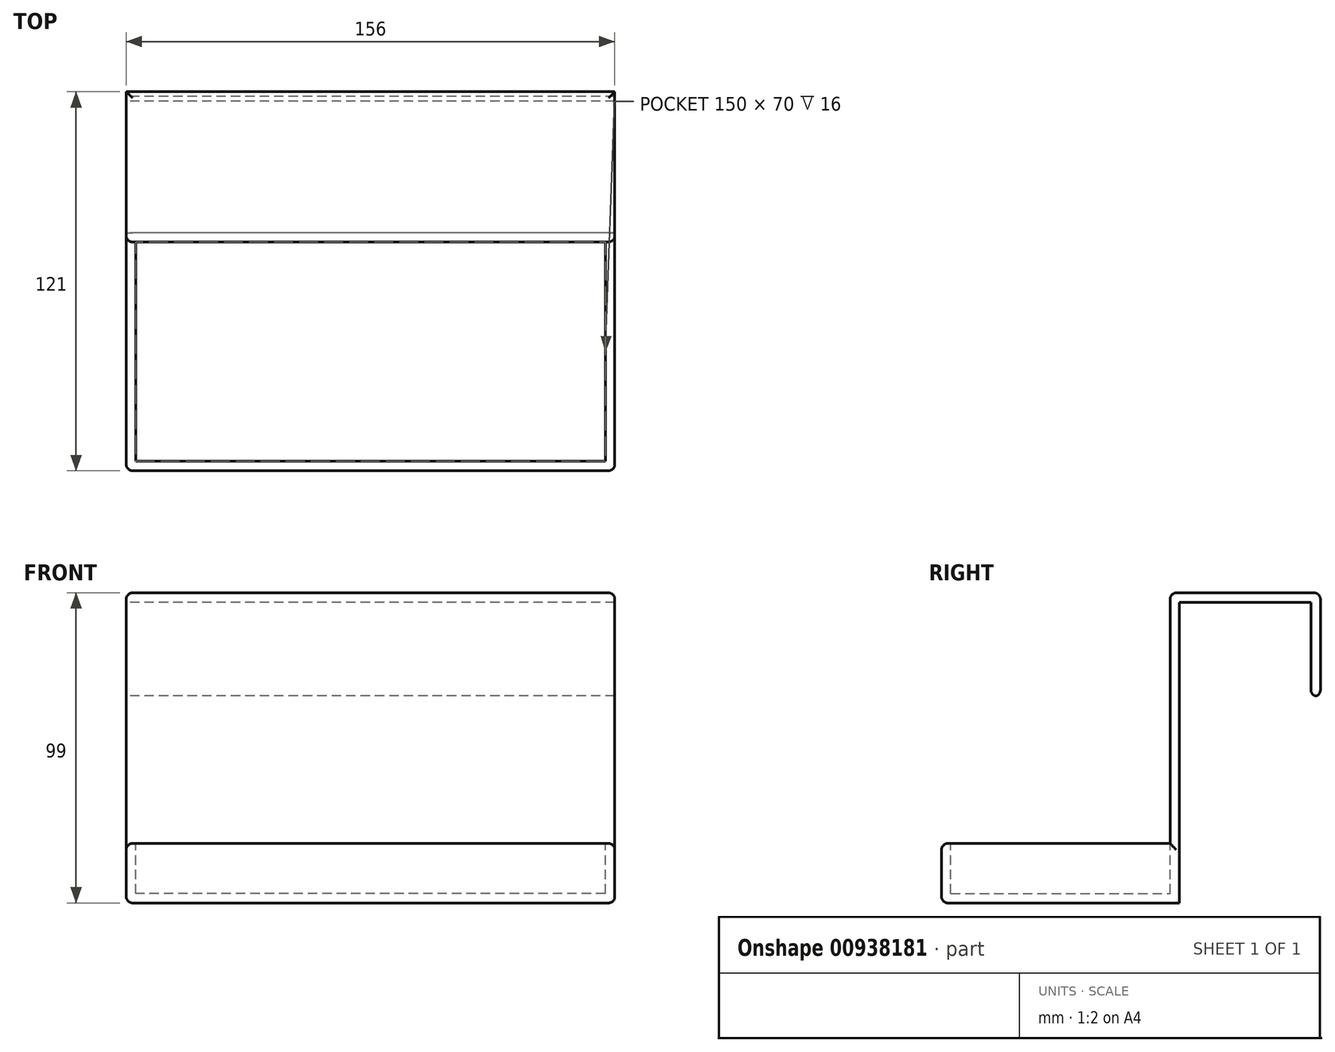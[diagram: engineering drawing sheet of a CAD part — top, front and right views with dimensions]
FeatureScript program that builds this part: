
annotation { "Feature Type Name" : "Feature", "Feature Type Description" : "" }
export const myFeature = defineFeature(function(context is Context, id is Id, definition is map)
    precondition{}
    {
        {
            var Q0;
            Q0=qCreatedBy(makeId("Right.planeOp"),FACE);
            var sketch = newSketch(context, id + "F0", { "sketchPlane" : qUnion([Q0])});
            skLineSegment(sketch, "E0", {"start": v(3, -3) * mm, "end": v(45, -3) * mm});
            skLineSegment(sketch, "E1", {"start": v(45, -3) * mm, "end": v(45, -33) * mm});
            skLineSegment(sketch, "E2", {"start": v(45, -33) * mm, "end": v(48, -33) * mm});
            skLineSegment(sketch, "E3", {"start": v(48, -33) * mm, "end": v(48, 0) * mm});
            skLineSegment(sketch, "E4", {"start": v(48, 0) * mm, "end": v(0, 0) * mm});
            skLineSegment(sketch, "E5", {"start": v(0, 0) * mm, "end": v(0, -80) * mm});
            skLineSegment(sketch, "E6", {"start": v(0, -80) * mm, "end": v(-73, -80) * mm});
            skLineSegment(sketch, "E7", {"start": v(-73, -80) * mm, "end": v(-73, -99) * mm});
            skLineSegment(sketch, "E8", {"start": v(-73, -99) * mm, "end": v(3, -99) * mm});
            skLineSegment(sketch, "E9", {"start": v(3, -99) * mm, "end": v(3, -3) * mm});
            skLineSegment(sketch, "E10", {"start": v(45, -3) * mm, "end": v(45, 0) * mm});
            skLineSegment(sketch, "E11", {"start": v(3, -3) * mm, "end": v(0, -3) * mm});
            skSolve(sketch);
        }
        {
            var Q0;
            {var subQ0=sQuery(id+"F0.wireOp",EDGE,"E6");Q0=makeQuery(id+"F0.imprint","IMPRINT",FACE,{"disambiguationData":[TD([[makeQuery(id+"F0.imprint","IMPRINT",EDGE,{"derivedFrom":subQ0}),1.0]])]});}
            var Q1;
            Q1=makeQuery(id+"F0.imprint","IMPRINT",FACE,{"disambiguationData":[TD([[makeQuery(id+"F0.imprint","IMPRINT",EDGE,{"derivedFrom":sQuery(id+"F0.wireOp",EDGE,"E0")}),1.0]])]});
            var Q2;
            Q2=makeQuery(id+"F0.imprint","IMPRINT",FACE,{"disambiguationData":[TD([[makeQuery(id+"F0.imprint","IMPRINT",EDGE,{"derivedFrom":sQuery(id+"F0.wireOp",EDGE,"E1")}),1.0]])]});
            extrude(context, id + "F1", {"entities" : qUnion([Q0, Q1, Q2]), "depth" : 156 * mm, "offsetDistance" : 25 * mm});
        }
        {
            var Q0;
            Q0=makeQuery(id+"F1.opExtrude","SWEPT_FACE",FACE,{"disambiguationData":[OSD([sQuery(id+"F0.wireOp",EDGE,"E6")])]});
            var sketch = newSketch(context, id + "F2", { "sketchPlane" : qUnion([Q0])});
            skLineSegment(sketch, "E12.bottom", {"start": v(3, -70) * mm, "end": v(153, -70) * mm});
            skLineSegment(sketch, "E12.top", {"start": v(3, 0) * mm, "end": v(153, 0) * mm});
            skLineSegment(sketch, "E12.left", {"start": v(3, -70) * mm, "end": v(3, 0) * mm});
            skLineSegment(sketch, "E12.right", {"start": v(153, -70) * mm, "end": v(153, 0) * mm});
            skLineSegment(sketch, "E13", {"start": v(3, -70) * mm, "end": v(3, -73) * mm});
            skLineSegment(sketch, "E14", {"start": v(3, -70) * mm, "end": v(0, -70) * mm});
            skLineSegment(sketch, "E15", {"start": v(153, -70) * mm, "end": v(156, -70) * mm});
            skSolve(sketch);
        }
        {
            var Q0;
            Q0=makeQuery(id+"F2.imprint","IMPRINT",FACE,{"disambiguationData":[TD([[makeQuery(id+"F2.imprint","IMPRINT",EDGE,{"derivedFrom":sQuery(id+"F2.wireOp",EDGE,"E12.bottom")}),1.0]])]});
            extrude(context, id + "F3", {"entities" : qUnion([Q0]), "operationType" : NewBodyOperationType.REMOVE, "oppositeDirection" : true, "depth" : 16 * mm, "offsetDistance" : 25 * mm});
        }
        {
            var Q0;
            Q0=makeQuery(id+"F1.opExtrude","SWEPT_EDGE",EDGE,{"disambiguationData":[OSD([sQuery(id+"F0.wireOp",EDGE,"E4"),sQuery(id+"F0.wireOp",EDGE,"E5")])]});
            var Q1;
            Q1=makeQuery(id+"F1.opExtrude","CAP_EDGE",EDGE,{"disambiguationData":[OSD([sQuery(id+"F0.wireOp",EDGE,"E4")])],"isStart":false});
            var Q2;
            Q2=makeQuery(id+"F1.opExtrude","SWEPT_EDGE",EDGE,{"disambiguationData":[OSD([sQuery(id+"F0.wireOp",EDGE,"E3"),sQuery(id+"F0.wireOp",EDGE,"E4")])]});
            var Q3;
            Q3=makeQuery(id+"F1.opExtrude","CAP_EDGE",EDGE,{"disambiguationData":[OSD([sQuery(id+"F0.wireOp",EDGE,"E4")])],"isStart":true});
            var Q4;
            Q4=makeQuery(id+"F1.opExtrude","SWEPT_EDGE",EDGE,{"disambiguationData":[OSD([sQuery(id+"F0.wireOp",EDGE,"E2"),sQuery(id+"F0.wireOp",EDGE,"E3")])]});
            var Q5;
            Q5=makeQuery(id+"F1.opExtrude","SWEPT_EDGE",EDGE,{"disambiguationData":[OSD([sQuery(id+"F0.wireOp",EDGE,"E1"),sQuery(id+"F0.wireOp",EDGE,"E2")])]});
            var Q6;
            Q6=makeQuery(id+"F1.opExtrude","CAP_EDGE",EDGE,{"disambiguationData":[OSD([sQuery(id+"F0.wireOp",EDGE,"E5")])],"isStart":false});
            var Q7;
            Q7=makeQuery(id+"F1.opExtrude","CAP_EDGE",EDGE,{"disambiguationData":[OSD([sQuery(id+"F0.wireOp",EDGE,"E5")])],"isStart":true});
            var Q8;
            Q8=makeQuery(id+"F1.opExtrude","CAP_EDGE",EDGE,{"disambiguationData":[OSD([sQuery(id+"F0.wireOp",EDGE,"E6")])],"isStart":false});
            var Q9;
            Q9=makeQuery(id+"F1.opExtrude","SWEPT_EDGE",EDGE,{"disambiguationData":[OSD([sQuery(id+"F0.wireOp",EDGE,"E6"),sQuery(id+"F0.wireOp",EDGE,"E7")])]});
            var Q10;
            Q10=makeQuery(id+"F1.opExtrude","CAP_EDGE",EDGE,{"disambiguationData":[OSD([sQuery(id+"F0.wireOp",EDGE,"E6")])],"isStart":true});
            var Q11;
            Q11=makeQuery(id+"F1.opExtrude","SWEPT_EDGE",EDGE,{"disambiguationData":[OSD([sQuery(id+"F0.wireOp",EDGE,"E7"),sQuery(id+"F0.wireOp",EDGE,"E8")])]});
            var Q12;
            Q12=makeQuery(id+"F1.opExtrude","CAP_EDGE",EDGE,{"disambiguationData":[OSD([sQuery(id+"F0.wireOp",EDGE,"E8")])],"isStart":false});
            var Q13;
            Q13=makeQuery(id+"F1.opExtrude","CAP_EDGE",EDGE,{"disambiguationData":[OSD([sQuery(id+"F0.wireOp",EDGE,"E8")])],"isStart":true});
            var Q14;
            Q14=makeQuery(id+"F1.opExtrude","CAP_EDGE",EDGE,{"disambiguationData":[OSD([sQuery(id+"F0.wireOp",EDGE,"E7")])],"isStart":true});
            var Q15;
            Q15=makeQuery(id+"F1.opExtrude","CAP_EDGE",EDGE,{"disambiguationData":[OSD([sQuery(id+"F0.wireOp",EDGE,"E7")])],"isStart":false});
            fillet(context, id + "F4", {"entities" : qUnion([Q0, Q1, Q2, Q3, Q4, Q5, Q6, Q7, Q8, Q9, Q10, Q11, Q12, Q13, Q14, Q15]), "radius" : 2 * mm, "tangentPropagation" : true, "allowEdgeOverflow" : false});
        }
    });
